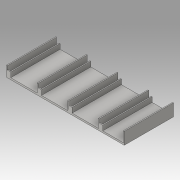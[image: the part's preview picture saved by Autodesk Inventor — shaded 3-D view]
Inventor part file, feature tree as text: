
AUTODESK INVENTOR PART (.ipt)
format: ipt  version: 2016 (Build 200138000, 138)  size: 234,496 bytes
history: native  units: in
note: dims shown in document units (in); Inventor stores cm internally (conversion verified against a paired STEP export)
features: sketch x15, extrude x14, fillet x4
ambient origin geometry x8: Origin, YZ Plane, XZ Plane, XY Plane, X Axis, Y Axis, Z Axis, Center Point
bodies: Solid1 (feature_tree)
feature tree (33):
  extrude  "Extrusion1"  Depth=3.4in TaperAngle=0.0deg
  extrude  "Extrusion2"  Depth=0.6in TaperAngle=0.0deg
  extrude  "Extrusion3"  Depth=0.34in TaperAngle=0.0deg
  extrude  "Extrusion4"  Depth=0.6in TaperAngle=0.0deg
  extrude  "Extrusion5"  Depth=0.34in TaperAngle=0.0deg
  extrude  "Extrusion6"  Depth=0.6in TaperAngle=0.0deg
  extrude  "Extrusion7"  Depth=0.34in TaperAngle=0.0deg
  extrude  "Extrusion8"  Depth=0.6in TaperAngle=0.0deg
  extrude  "Extrusion9"  Depth=0.34in TaperAngle=0.0deg
  extrude  "Extrusion10"  Depth=0.34in TaperAngle=0.0deg
  extrude  "Extrusion11"  Depth=0.34in TaperAngle=0.0deg
  extrude  "Extrusion12"  Depth=0.063in
  extrude  "Extrusion13"  Depth=0.09in
  sketch  "Sketch14"  dims[d40=0.09in d41=0.09in d42=0.09in]
  extrude  "Extrusion14"  Depth=0.09in
  fillet  "Fillet1"  Radius=0.09in
  fillet  "Fillet2"  [1 undecoded]
  fillet  "Fillet3"  [1 undecoded]
  fillet  "Fillet4"  [1 undecoded]
  sketch  "Sketch1"  dims[d0=8.126in d1=3.4in d2=0.0in]
  sketch  "Sketch2"  dims[d3=0.063in d4=0.6in d5=0.0in]
  sketch  "Sketch3"  dims[d6=0.063in d7=0.34in d8=0.0in]
  sketch  "Sketch4"  dims[d9=0.063in d10=0.6in d11=0.0in]
  sketch  "Sketch5"  dims[d12=0.063in d13=0.34in d14=0.0in]
  sketch  "Sketch6"  dims[d15=0.063in d16=0.6in d17=0.0in]
  sketch  "Sketch7"  dims[d18=0.063in d19=0.34in d20=0.0in]
  sketch  "Sketch8"  dims[d21=0.063in d22=0.6in d23=0.0in]
  sketch  "Sketch9"  dims[d24=0.063in d25=0.34in d26=0.0in]
  sketch  "Sketch10"  dims[d27=0.063in d28=0.34in d29=0.0in]
  sketch  "Sketch11"  dims[d30=0.34in d31=0.0in d32=0.34in d33=0.0in]
  sketch  "Sketch12"  dims[d34=0.34in d35=0.0in d36=0.063in]
  sketch  "Sketch13"  dims[d37=0.718in d38=0.0in d39=0.09in]
  sketch  "Sketch15"
note: 3 required parameter values undecoded (feature->parameter linkage not recoverable at this tier; creation-order binding heuristic only, values carry confidence <= 0.55)
